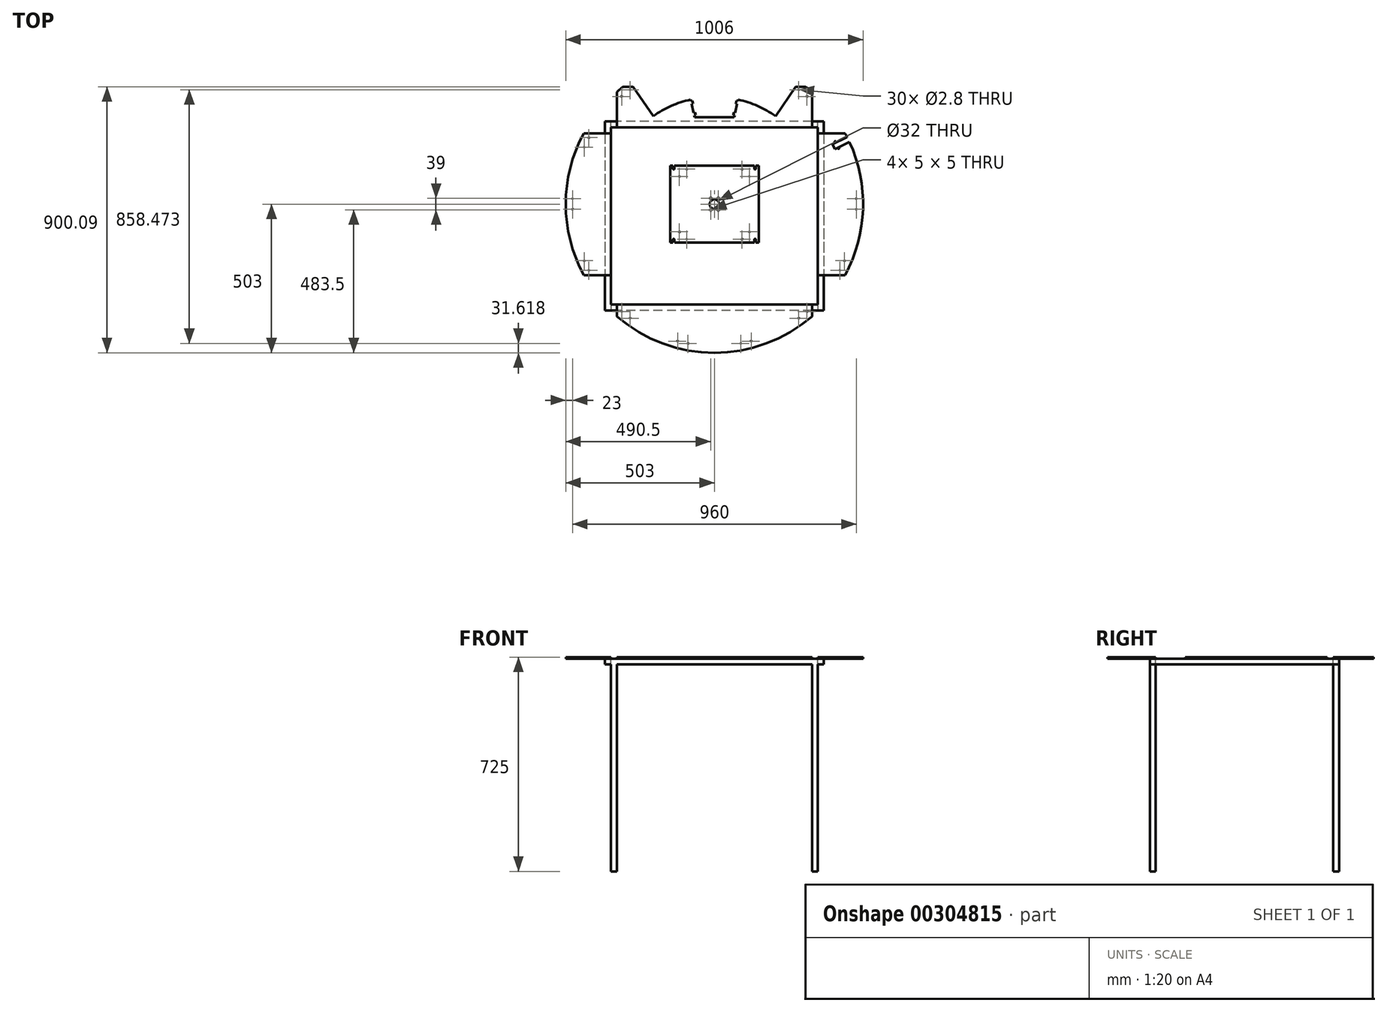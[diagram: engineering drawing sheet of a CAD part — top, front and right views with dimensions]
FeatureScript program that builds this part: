
annotation { "Feature Type Name" : "Feature", "Feature Type Description" : "" }
export const myFeature = defineFeature(function(context is Context, id is Id, definition is map)
    precondition{}
    {
        {
            var Q0;
            Q0=qCreatedBy(makeId("Top.planeOp"),FACE);
            var sketch = newSketch(context, id + "F0", { "sketchPlane" : qUnion([Q0])});
            skCircle(sketch, "E0", {"center": v(480, 18.59) * mm, "radius": 1.4 * mm});
            skCircle(sketch, "E1.MirrorC", {"center": v(480, -17.41) * mm, "radius": 1.4 * mm});
            skCircle(sketch, "E2.2.0", {"center": v(285.2, 387.1) * mm, "radius": 1.4 * mm});
            skCircle(sketch, "E2.2.1", {"center": v(313.35, 364.64) * mm, "radius": 1.4 * mm});
            skCircle(sketch, "E2.5.0", {"center": v(-313.35, 364.64) * mm, "radius": 1.4 * mm});
            skCircle(sketch, "E2.5.1", {"center": v(-285.2, 387.1) * mm, "radius": 1.4 * mm});
            skCircle(sketch, "E2.6.0", {"center": v(-440.27, 192.64) * mm, "radius": 1.4 * mm});
            skCircle(sketch, "E2.6.1", {"center": v(-424.66, 225.07) * mm, "radius": 1.4 * mm});
            skCircle(sketch, "E2.7.0", {"center": v(-480, -17.41) * mm, "radius": 1.4 * mm});
            skCircle(sketch, "E2.7.1", {"center": v(-480, 18.59) * mm, "radius": 1.4 * mm});
            skCircle(sketch, "E2.8.0", {"center": v(-424.66, -223.9) * mm, "radius": 1.4 * mm});
            skCircle(sketch, "E2.8.1", {"center": v(-440.27, -191.46) * mm, "radius": 1.4 * mm});
            skCircle(sketch, "E2.9.0", {"center": v(-285.2, -385.91) * mm, "radius": 1.4 * mm});
            skCircle(sketch, "E2.9.1", {"center": v(-313.35, -363.47) * mm, "radius": 1.4 * mm});
            skCircle(sketch, "E2.10.0", {"center": v(-89.26, -471.38) * mm, "radius": 1.4 * mm});
            skCircle(sketch, "E2.10.1", {"center": v(-124.36, -463.37) * mm, "radius": 1.4 * mm});
            skCircle(sketch, "E2.11.0", {"center": v(124.36, -463.37) * mm, "radius": 1.4 * mm});
            skCircle(sketch, "E2.11.1", {"center": v(89.26, -471.38) * mm, "radius": 1.4 * mm});
            skCircle(sketch, "E2.12.0", {"center": v(313.35, -363.47) * mm, "radius": 1.4 * mm});
            skCircle(sketch, "E2.12.1", {"center": v(285.2, -385.91) * mm, "radius": 1.4 * mm});
            skCircle(sketch, "E2.13.0", {"center": v(440.27, -191.46) * mm, "radius": 1.4 * mm});
            skCircle(sketch, "E2.13.1", {"center": v(424.66, -223.9) * mm, "radius": 1.4 * mm});
            skLineSegment(sketch, "E3", {"start": v(-330, -340) * mm, "end": v(-330, -379.62) * mm});
            skLineSegment(sketch, "E4", {"start": v(330, 368.95) * mm, "end": v(330, 260) * mm});
            skLineSegment(sketch, "E5.trimOffspring", {"start": v(350, 240) * mm, "end": v(442.05, 240) * mm});
            skLineSegment(sketch, "E6.trimOffspring", {"start": v(350, -240) * mm, "end": v(442.05, -240) * mm});
            skPoint(sketch, "E7.middle", {"position": v(0, -64.22) * mm});
            skLineSegment(sketch, "E8", {"start": v(330, 379.62) * mm, "end": v(330, 260) * mm});
            skLineSegment(sketch, "E9", {"start": v(-275.2, 397.1) * mm, "end": v(-308.75, 397.1) * mm});
            skLineSegment(sketch, "E10", {"start": v(-330, 379.62) * mm, "end": v(-330, 260) * mm});
            skLineSegment(sketch, "E11", {"start": v(-350, 240) * mm, "end": v(-442.05, 240) * mm});
            skLineSegment(sketch, "E12", {"start": v(-442.05, -240) * mm, "end": v(-350, -240) * mm});
            skArc(sketch, "E13", {"start": v(330, 379.62) * mm, "mid": v(319.5, 388.5) * mm, "end": v(308.75, 397.1) * mm});
            skPoint(sketch, "E14.middle", {"position": v(0, -10) * mm});
            skPoint(sketch, "E15.orphan", {"position": v(-330, 397.1) * mm});
            skPoint(sketch, "E16.orphan", {"position": v(330, 400) * mm});
            skArc(sketch, "E17.trimOffspring", {"start": v(-442.05, 240) * mm, "mid": v(-503, 0) * mm, "end": v(-442.05, -240) * mm});
            skArc(sketch, "E18.trimOffspring", {"start": v(-308.75, 397.1) * mm, "mid": v(-319.5, 388.5) * mm, "end": v(-330, 379.62) * mm});
            skArc(sketch, "E19.trimOffspring", {"start": v(-330, -379.62) * mm, "mid": v(0, -503) * mm, "end": v(330, -379.62) * mm});
            skArc(sketch, "E20.trimOffspring", {"start": v(442.05, -240) * mm, "mid": v(502.73, -16.45) * mm, "end": v(456.8, 210.58) * mm});
            skLineSegment(sketch, "E21.trimOffspring", {"start": v(330, -340) * mm, "end": v(330, -379.62) * mm});
            skLineSegment(sketch, "E22", {"start": v(-350, 240) * mm, "end": v(-350, -240) * mm});
            skLineSegment(sketch, "E23", {"start": v(-330, 260) * mm, "end": v(330, 260) * mm});
            skLineSegment(sketch, "E24", {"start": v(350, 240) * mm, "end": v(350, -240) * mm});
            skLineSegment(sketch, "E25", {"start": v(-330, -340) * mm, "end": v(330, -340) * mm});
            skLineSegment(sketch, "E26.bottom", {"start": v(-150, 130) * mm, "end": v(-140, 130) * mm});
            skCircle(sketch, "E27.7.0", {"center": v(93.7, 118.44) * mm, "radius": 1.4 * mm});
            skCircle(sketch, "E27.7.1", {"center": v(118.44, 93.7) * mm, "radius": 1.4 * mm});
            skArc(sketch, "E28", {"start": v(-140, 120) * mm, "mid": v(-137.5, 117.5) * mm, "end": v(-135, 120) * mm});
            skLineSegment(sketch, "E29", {"start": v(-140, 120) * mm, "end": v(-140, 130) * mm});
            skLineSegment(sketch, "E30", {"start": v(-135, 120) * mm, "end": v(-135, 130) * mm});
            skLineSegment(sketch, "E31.trimOffspring", {"start": v(-135, 130) * mm, "end": v(135, 130) * mm});
            skLineSegment(sketch, "E32.MirrorCS", {"start": v(140, 120) * mm, "end": v(140, 130) * mm});
            skLineSegment(sketch, "E33.MirrorCS", {"start": v(135, 120) * mm, "end": v(135, 130) * mm});
            skLineSegment(sketch, "E34.trimOffspring", {"start": v(140, 130) * mm, "end": v(150, 130) * mm});
            skArc(sketch, "E35", {"start": v(135, 120) * mm, "mid": v(137.5, 117.5) * mm, "end": v(140, 120) * mm});
            skLineSegment(sketch, "E36", {"start": v(-150, -130) * mm, "end": v(-140, -130) * mm});
            skLineSegment(sketch, "E37", {"start": v(-150, 130) * mm, "end": v(-150, -130) * mm});
            skLineSegment(sketch, "E38", {"start": v(150, 130) * mm, "end": v(150, -130) * mm});
            skPoint(sketch, "E39", {"position": v(150, 0) * mm});
            skCircle(sketch, "E40.1.0", {"center": v(-93.7, 118.44) * mm, "radius": 1.4 * mm});
            skCircle(sketch, "E40.1.1", {"center": v(-118.44, 93.7) * mm, "radius": 1.4 * mm});
            skCircle(sketch, "E40.2.0", {"center": v(-118.44, -93.7) * mm, "radius": 1.4 * mm});
            skCircle(sketch, "E40.2.1", {"center": v(-93.7, -118.44) * mm, "radius": 1.4 * mm});
            skCircle(sketch, "E40.3.0", {"center": v(93.7, -118.44) * mm, "radius": 1.4 * mm});
            skCircle(sketch, "E40.3.1", {"center": v(118.44, -93.7) * mm, "radius": 1.4 * mm});
            skLineSegment(sketch, "E41", {"start": v(-275.2, 397.1) * mm, "end": v(-206.77, 298.35) * mm});
            skLineSegment(sketch, "E42", {"start": v(308.75, 397.1) * mm, "end": v(275.2, 397.1) * mm});
            skLineSegment(sketch, "E43.trimOffspring", {"start": v(206.77, 298.35) * mm, "end": v(275.2, 397.1) * mm});
            skLineSegment(sketch, "E44", {"start": v(-80.5, 353.96) * mm, "end": v(-67.04, 294.47) * mm});
            skLineSegment(sketch, "E45", {"start": v(67.04, 294.47) * mm, "end": v(80.5, 353.96) * mm});
            skLineSegment(sketch, "E46", {"start": v(-79.4, 349.09) * mm, "end": v(-74.52, 350.19) * mm});
            skLineSegment(sketch, "E47", {"start": v(-74.52, 350.19) * mm, "end": v(-72.31, 340.44) * mm});
            skLineSegment(sketch, "E48", {"start": v(-72.31, 340.44) * mm, "end": v(-77.19, 339.33) * mm});
            skLineSegment(sketch, "E49", {"start": v(-70.57, 310.07) * mm, "end": v(-65.7, 311.18) * mm});
            skLineSegment(sketch, "E50", {"start": v(-65.7, 311.18) * mm, "end": v(-63.48, 301.42) * mm});
            skLineSegment(sketch, "E51", {"start": v(-63.48, 301.42) * mm, "end": v(-68.36, 300.32) * mm});
            skLineSegment(sketch, "E52", {"start": v(79.4, 349.09) * mm, "end": v(74.52, 350.19) * mm});
            skLineSegment(sketch, "E53", {"start": v(74.52, 350.19) * mm, "end": v(72.31, 340.44) * mm});
            skLineSegment(sketch, "E54", {"start": v(72.31, 340.44) * mm, "end": v(77.19, 339.33) * mm});
            skLineSegment(sketch, "E55", {"start": v(70.57, 310.07) * mm, "end": v(65.7, 311.18) * mm});
            skLineSegment(sketch, "E56", {"start": v(65.7, 311.18) * mm, "end": v(63.48, 301.42) * mm});
            skLineSegment(sketch, "E57", {"start": v(63.48, 301.42) * mm, "end": v(68.36, 300.32) * mm});
            skPoint(sketch, "E58", {"position": v(-67.04, 294.47) * mm});
            skLineSegment(sketch, "E59", {"start": v(-67.04, 294.47) * mm, "end": v(67.04, 294.47) * mm});
            skArc(sketch, "E60.trimOffspring", {"start": v(-80.5, 353.96) * mm, "mid": v(-146.3, 332.21) * mm, "end": v(-206.77, 298.35) * mm});
            skArc(sketch, "E61.trimOffspring", {"start": v(206.77, 298.35) * mm, "mid": v(146.3, 332.21) * mm, "end": v(80.5, 353.96) * mm});
            skLineSegment(sketch, "E62.bottom", {"start": v(-15, 22) * mm, "end": v(-10, 22) * mm});
            skLineSegment(sketch, "E62.top", {"start": v(-15, 17) * mm, "end": v(-10, 17) * mm});
            skLineSegment(sketch, "E62.left", {"start": v(-15, 22) * mm, "end": v(-15, 17) * mm});
            skLineSegment(sketch, "E62.right", {"start": v(-10, 22) * mm, "end": v(-10, 17) * mm});
            skLineSegment(sketch, "E63.bottom", {"start": v(10, 22) * mm, "end": v(15, 22) * mm});
            skLineSegment(sketch, "E63.top", {"start": v(10, 17) * mm, "end": v(15, 17) * mm});
            skLineSegment(sketch, "E63.left", {"start": v(10, 22) * mm, "end": v(10, 17) * mm});
            skLineSegment(sketch, "E63.right", {"start": v(15, 22) * mm, "end": v(15, 17) * mm});
            skLineSegment(sketch, "E64.bottom", {"start": v(-15, -17) * mm, "end": v(-10, -17) * mm});
            skLineSegment(sketch, "E64.top", {"start": v(-15, -22) * mm, "end": v(-10, -22) * mm});
            skLineSegment(sketch, "E64.left", {"start": v(-15, -17) * mm, "end": v(-15, -22) * mm});
            skLineSegment(sketch, "E64.right", {"start": v(-10, -17) * mm, "end": v(-10, -22) * mm});
            skLineSegment(sketch, "E65.bottom", {"start": v(10, -17) * mm, "end": v(15, -17) * mm});
            skLineSegment(sketch, "E65.top", {"start": v(10, -22) * mm, "end": v(15, -22) * mm});
            skLineSegment(sketch, "E65.left", {"start": v(10, -17) * mm, "end": v(10, -22) * mm});
            skLineSegment(sketch, "E65.right", {"start": v(15, -17) * mm, "end": v(15, -22) * mm});
            skCircle(sketch, "E66", {"center": v(0, 0) * mm, "radius": 16 * mm});
            skPoint(sketch, "E67", {"position": v(432.47, 208.85) * mm});
            skPoint(sketch, "E68.1.0", {"position": v(299.02, 375.8) * mm});
            skPoint(sketch, "E68.2.0", {"position": v(106.35, 468.33) * mm});
            skPoint(sketch, "E68.3.0", {"position": v(-107.38, 468.1) * mm});
            skPoint(sketch, "E68.4.0", {"position": v(-299.85, 375.15) * mm});
            skPoint(sketch, "E68.5.0", {"position": v(-432.92, 207.9) * mm});
            skPoint(sketch, "E68.6.0", {"position": v(-480.26, -0.53) * mm});
            skPoint(sketch, "E68.7.0", {"position": v(-432.47, -208.85) * mm});
            skPoint(sketch, "E68.8.0", {"position": v(-299.02, -375.8) * mm});
            skPoint(sketch, "E68.9.0", {"position": v(-106.35, -468.33) * mm});
            skPoint(sketch, "E68.10.0", {"position": v(107.38, -468.1) * mm});
            skPoint(sketch, "E68.11.0", {"position": v(299.85, -375.15) * mm});
            skPoint(sketch, "E68.12.0", {"position": v(432.92, -207.9) * mm});
            skPoint(sketch, "E68.13.0", {"position": v(480.26, 0.53) * mm});
            skLineSegment(sketch, "E69", {"start": v(399.73, 203.08) * mm, "end": v(407.54, 186.86) * mm});
            skLineSegment(sketch, "E70", {"start": v(407.54, 186.86) * mm, "end": v(461.6, 212.9) * mm});
            skLineSegment(sketch, "E71", {"start": v(453.79, 229.1) * mm, "end": v(399.73, 203.08) * mm});
            skPoint(sketch, "E72", {"position": v(434.57, 199.88) * mm});
            skPoint(sketch, "E73", {"position": v(461.3, 222.74) * mm});
            skLineSegment(sketch, "E74", {"start": v(461.3, 222.74) * mm, "end": v(403.63, 194.97) * mm});
            skCircle(sketch, "E75", {"center": v(419.87, 188.91) * mm, "radius": 1.9 * mm});
            skCircle(sketch, "E76", {"center": v(409.02, 211.44) * mm, "radius": 1.9 * mm});
            skPoint(sketch, "E77", {"position": v(414.45, 200.17) * mm});
            skArc(sketch, "E78.trimOffspring", {"start": v(448.97, 226.8) * mm, "mid": v(445.56, 233.42) * mm, "end": v(442.05, 240) * mm});
            skLineSegment(sketch, "E79", {"start": v(-140, -130) * mm, "end": v(-140, -120) * mm});
            skLineSegment(sketch, "E80", {"start": v(-135, -120) * mm, "end": v(-134.8, -130) * mm});
            skLineSegment(sketch, "E81", {"start": v(135, -130) * mm, "end": v(135, -120) * mm});
            skLineSegment(sketch, "E82", {"start": v(140, -120) * mm, "end": v(140, -130) * mm});
            skArc(sketch, "E83", {"start": v(-135, -120) * mm, "mid": v(-137.5, -117.5) * mm, "end": v(-140, -120) * mm});
            skArc(sketch, "E84", {"start": v(140, -120) * mm, "mid": v(137.5, -117.5) * mm, "end": v(135, -120) * mm});
            skLineSegment(sketch, "E85.trimOffspring", {"start": v(-134.8, -130) * mm, "end": v(135, -130) * mm});
            skLineSegment(sketch, "E86.trimOffspring", {"start": v(140, -130) * mm, "end": v(150, -130) * mm});
            skSolve(sketch);
        }
        {
            var Q0;
            Q0=qCreatedBy(makeId("Top.planeOp"),FACE);
            var sketch = newSketch(context, id + "F1", { "sketchPlane" : qUnion([Q0])});
            skLineSegment(sketch, "E87.bottom", {"start": v(370, 280) * mm, "end": v(-370, 280) * mm});
            skLineSegment(sketch, "E87.top", {"start": v(370, -360) * mm, "end": v(-370, -360) * mm});
            skLineSegment(sketch, "E87.left", {"start": v(370, 280) * mm, "end": v(370, -360) * mm});
            skLineSegment(sketch, "E87.right", {"start": v(-370, 280) * mm, "end": v(-370, -360) * mm});
            skLineSegment(sketch, "E88.bottom", {"start": v(-350, 260) * mm, "end": v(350, 260) * mm});
            skLineSegment(sketch, "E88.top", {"start": v(-350, -340) * mm, "end": v(350, -340) * mm});
            skLineSegment(sketch, "E88.left", {"start": v(-350, 260) * mm, "end": v(-350, -340) * mm});
            skLineSegment(sketch, "E88.right", {"start": v(350, 260) * mm, "end": v(350, -340) * mm});
            skLineSegment(sketch, "E89.bottom", {"start": v(-127.5, 260) * mm, "end": v(-147.5, 260) * mm});
            skLineSegment(sketch, "E89.top", {"start": v(-127.5, -340) * mm, "end": v(-147.5, -340) * mm});
            skLineSegment(sketch, "E89.left", {"start": v(-127.5, 260) * mm, "end": v(-127.5, -340) * mm});
            skLineSegment(sketch, "E89.right", {"start": v(-147.5, 260) * mm, "end": v(-147.5, -340) * mm});
            skPoint(sketch, "E89.middle", {"position": v(-137.5, -40) * mm});
            skLineSegment(sketch, "E90.bottom", {"start": v(147.5, 260) * mm, "end": v(127.5, 260) * mm});
            skLineSegment(sketch, "E90.top", {"start": v(147.5, -340) * mm, "end": v(127.5, -340) * mm});
            skLineSegment(sketch, "E90.left", {"start": v(147.5, 260) * mm, "end": v(147.5, -340) * mm});
            skLineSegment(sketch, "E90.right", {"start": v(127.5, 260) * mm, "end": v(127.5, -340) * mm});
            skPoint(sketch, "E90.middle", {"position": v(137.5, -40) * mm});
            skSolve(sketch);
        }
        {
            var Q0;
            Q0 = qSketchRegion(id + "F1", true);
            var Q1;
            Q1=makeQuery(id+"F1.imprint","IMPRINT",FACE,{"disambiguationData":[TD([[makeQuery(id+"F1.imprint","IMPRINT",EDGE,{"derivedFrom":sQuery(id+"F1.wireOp",EDGE,"E90.bottom")}),1.0]])]});
            var Q2;
            Q2=makeQuery(id+"F1.imprint","IMPRINT",FACE,{"disambiguationData":[TD([[makeQuery(id+"F1.imprint","IMPRINT",EDGE,{"derivedFrom":sQuery(id+"F1.wireOp",EDGE,"E89.bottom")}),1.0]])]});
            extrude(context, id + "F2", {"entities" : qUnion([Q0, Q1, Q2]), "oppositeDirection" : true, "depth" : 20 * mm});
        }
        {
            var Q0;
            Q0 = qSketchRegion(id + "F0", true);
            extrude(context, id + "F3", {"entities" : qUnion([Q0]), "operationType" : NewBodyOperationType.ADD, "depth" : 5 * mm});
        }
        {
            var Q0;
            Q0=makeQuery(id+"F2.opExtrude","CAP_FACE",FACE,{"disambiguationData":[OSD([sQuery(id+"F1.wireOp",EDGE,"E87.bottom"),sQuery(id+"F1.wireOp",EDGE,"E87.top"),sQuery(id+"F1.wireOp",EDGE,"E87.left"),sQuery(id+"F1.wireOp",EDGE,"E87.right"),sQuery(id+"F1.wireOp",EDGE,"E88.bottom"),sQuery(id+"F1.wireOp",EDGE,"E88.top"),sQuery(id+"F1.wireOp",EDGE,"E88.left"),sQuery(id+"F1.wireOp",EDGE,"E88.right"),sQuery(id+"F1.wireOp",EDGE,"017a941e-ffe1-4023-9c4f-c7ee4791e156.left"),sQuery(id+"F1.wireOp",EDGE,"017a941e-ffe1-4023-9c4f-c7ee4791e156.right"),sQuery(id+"F1.wireOp",EDGE,"947ada8d-4a05-4e0a-ad06-175640b1956a.MirrorCS"),sQuery(id+"F1.wireOp",EDGE,"43dcbead-31ef-4f10-976b-8d890396d610.MirrorCS")])],"isStart":false});
            var sketch = newSketch(context, id + "F4", { "sketchPlane" : qUnion([Q0])});
            skLineSegment(sketch, "E91.bottom", {"start": v(-350, 340) * mm, "end": v(-330, 340) * mm});
            skLineSegment(sketch, "E91.top", {"start": v(-350, 360) * mm, "end": v(-330, 360) * mm});
            skLineSegment(sketch, "E91.left", {"start": v(-350, 340) * mm, "end": v(-350, 360) * mm});
            skLineSegment(sketch, "E91.right", {"start": v(-330, 340) * mm, "end": v(-330, 360) * mm});
            skLineSegment(sketch, "E92.bottom", {"start": v(350, 340) * mm, "end": v(330, 340) * mm});
            skLineSegment(sketch, "E92.top", {"start": v(350, 360) * mm, "end": v(330, 360) * mm});
            skLineSegment(sketch, "E92.left", {"start": v(350, 340) * mm, "end": v(350, 360) * mm});
            skLineSegment(sketch, "E92.right", {"start": v(330, 340) * mm, "end": v(330, 360) * mm});
            skLineSegment(sketch, "E93.bottom", {"start": v(-350, -260) * mm, "end": v(-330, -260) * mm});
            skLineSegment(sketch, "E93.top", {"start": v(-350, -280) * mm, "end": v(-330, -280) * mm});
            skLineSegment(sketch, "E93.left", {"start": v(-350, -260) * mm, "end": v(-350, -280) * mm});
            skLineSegment(sketch, "E93.right", {"start": v(-330, -260) * mm, "end": v(-330, -280) * mm});
            skLineSegment(sketch, "E94.bottom", {"start": v(350, -260) * mm, "end": v(330, -260) * mm});
            skLineSegment(sketch, "E94.top", {"start": v(350, -280) * mm, "end": v(330, -280) * mm});
            skLineSegment(sketch, "E94.left", {"start": v(350, -260) * mm, "end": v(350, -280) * mm});
            skLineSegment(sketch, "E94.right", {"start": v(330, -260) * mm, "end": v(330, -280) * mm});
            skSolve(sketch);
        }
        {
            var Q0;
            Q0 = qSketchRegion(id + "F4", true);
            extrude(context, id + "F5", {"entities" : qUnion([Q0]), "operationType" : NewBodyOperationType.ADD, "depth" : 700 * mm});
        }
    });
